# Revit family: 1770 Swoon Lounge
name_source: partatom
category: Furniture
revit_build: Autodesk Revit 2017 (Build: 20171027_0315(x64)
units: mm (PartAtom-declared; Revit-internal decimal feet)

## family parameters
Always vertical = Yes
Cut with Voids When Loaded = No
OmniClass Number = 23.40.20.00
OmniClass Title = General Furniture and Specialties
Room Calculation Point = No
Shared = No
Work Plane-Based = No

## types (1)
- 1770 Swoon Lounge
    Back Cushion = FF Sunniva 717
    Depth = 90 cm
    Description = Swoon is a comfortable yet sophisticated easy chair designed for lounge areas and private homes. Designed by Space Copenhagen in 2016, the chair stylishly combines an injection-moulded shell upholstered in either leather or fabric and soft fabric cushions.
    Design year = 2015
    Designer = Space Copenhagen
    Height = 83,5 cm
    Item No. = 1770
    Legs = FF Oak Black vertical
    Manufacturer = Fredericia Furniture
    Model = Swoon Lounge
    Seat Cushion = FF Sunniva 717
    Seat Height = 41,5 cm
    Shell Modify = Change Shell Upholstery in Manage -> Object Styles ->Imported Objects
    URL = https://www.fredericia.com
    Variation Legs = Available in other kind of wood
    Variations Upholster = Cuchion available in textile. Shell available in fabric and leather
    Weight = 17 kg
    Width = 88,5 cm

## geometry (parser evidence)
native form markers: Sweep x2
no freeform markers — native parametric forms only
